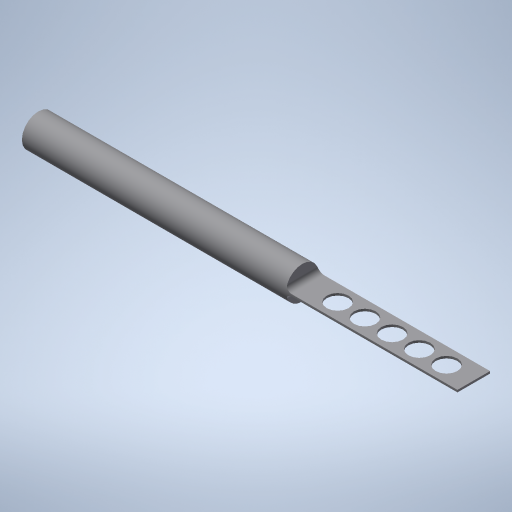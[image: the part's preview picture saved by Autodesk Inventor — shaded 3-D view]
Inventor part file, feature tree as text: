
AUTODESK INVENTOR PART (.ipt)
format: ipt  version: 2023.2 (Build 272271000, 271)  size: 305,152 bytes
history: native  units: mm
features: sketch x5, extrude x3, projected_geometry x3, plane x2, hole x1, pattern_linear x1
ambient origin geometry x8: Origin, YZ Plane, XZ Plane, XY Plane, X Axis, Y Axis, Z Axis, Center Point
bodies: Solid1 (feature_tree)
feature tree (15):
  extrude  "Extrusion1"  Depth=71.0mm TaperAngle=0.0deg
  plane  "Work Plane1"
  hole  "Hole1"  [1 undecoded]
  pattern_linear  "Rectangular Pattern1"  Spacing1=27.5mm  [1 undecoded]
  extrude  "Extrusion2"  Depth=0.5mm
  plane  "Work Plane2"
  sketch  "Sketch4"  dims[d9=2.0mm]
  extrude  "Extrusion3"  Depth=0.5mm
  sketch  "Sketch1"  dims[d0=3.0mm d1=71.0mm d2=0.0mm]
  sketch  "Sketch2"  dims[d3=0.5mm d4=0.2mm]
  projected_geometry  "Projected Loop1"
  sketch  "Sketch3"  dims[d5=0.0mm d6=0.0mm]
  projected_geometry  "Projected Loop2"
  sketch  "Sketch5"  dims[d10=6.0mm d11=4.0mm d12=2.0mm d13=90.0deg d14=0.15mm d15=20.594885mm d16=27.5mm d17=50.0mm d19=2.5mm d20=16.5mm d21=24.25mm d22=45.0deg d23=0.7032mm d24=1.12512mm d25=1.41312mm d26=1.035mm d27=0.5175mm d28=0.70656mm d29=31.0mm d30=0.0mm d31=0.5mm d32=0.872665mm]
  projected_geometry  "Projected Loop3"
note: 2 required parameter values undecoded (feature->parameter linkage not recoverable at this tier; creation-order binding heuristic only, values carry confidence <= 0.55)
